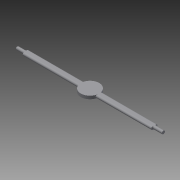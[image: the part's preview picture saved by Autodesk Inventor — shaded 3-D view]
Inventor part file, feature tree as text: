
AUTODESK INVENTOR PART (.ipt)
format: ipt  version: 2015 (Build 190159000, 159)  size: 187,392 bytes
history: native  units: in
note: dims shown in document units (in); Inventor stores cm internally (conversion verified against a paired STEP export)
features: extrude x4, fillet x4, sketch x4
ambient origin geometry x8: Origin, YZ Plane, XZ Plane, XY Plane, X Axis, Y Axis, Z Axis, Center Point
bodies: Solid1 (feature_tree)
feature tree (12):
  extrude  "Extrusion1"  Depth=0.5in
  extrude  "Extrusion2"  Depth=0.25in
  extrude  "Extrusion3"  Depth=1.5in
  extrude  "Extrusion4"  Depth=0.25in
  fillet  "Fillet1"  Radius=0.125in
  fillet  "Fillet2"  Radius=0.75in
  fillet  "Fillet3"  Radius=0.125in
  fillet  "Fillet4"  Radius=0.25in
  sketch  "Sketch1"  dims[d0=10.5in d1=0.5in]
  sketch  "Sketch2"  dims[d2=0.25in d3=0.0in d4=0.25in]
  sketch  "Sketch3"  dims[d5=5.25in d6=1.5in]
  sketch  "Sketch4"  dims[d7=0.25in d8=0.0in d9=0.25in d10=0.125in d11=0.75in d12=0.0in d13=0.125in d14=0.25in d15=0.75in d16=0.0in d17=0.125in d18=0.125in d19=0.125in d20=0.125in]
